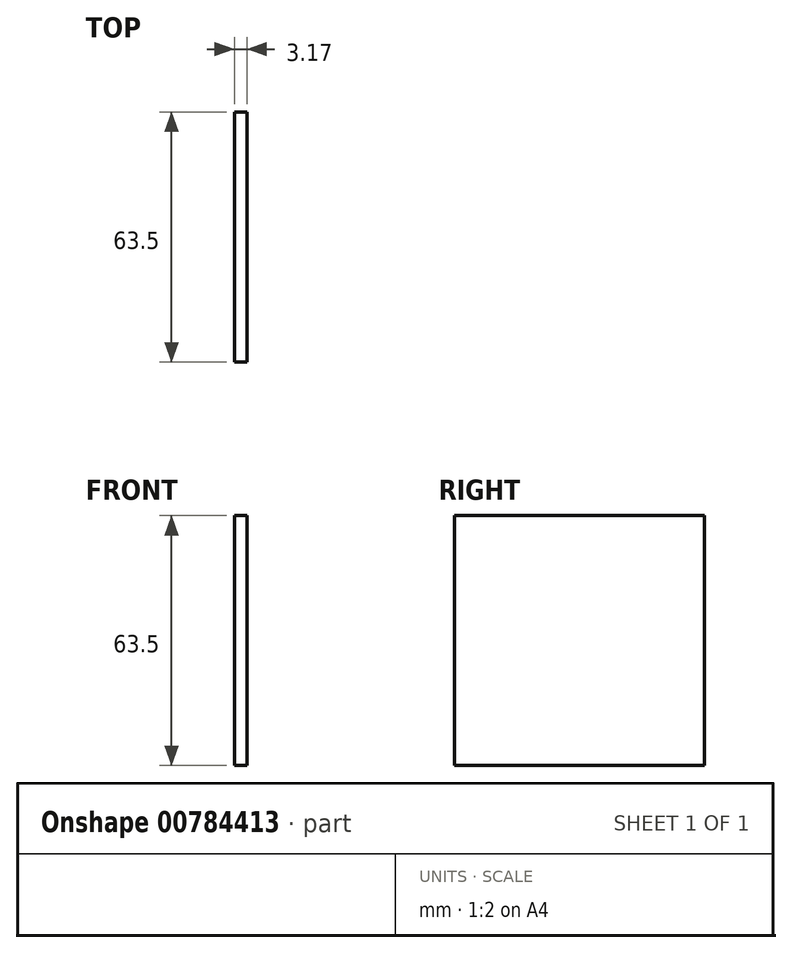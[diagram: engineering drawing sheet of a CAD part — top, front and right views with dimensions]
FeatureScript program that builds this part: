
annotation { "Feature Type Name" : "Feature", "Feature Type Description" : "" }
export const myFeature = defineFeature(function(context is Context, id is Id, definition is map)
    precondition{}
    {
        {
            var Q0;
            Q0=qCreatedBy(makeId("Right.planeOp"),FACE);
            var sketch = newSketch(context, id + "F0", { "sketchPlane" : qUnion([Q0])});
            skLineSegment(sketch, "E0.bottom", {"start": v(-29.8, 31) * mm, "end": v(33.7, 31) * mm});
            skLineSegment(sketch, "E0.top", {"start": v(-29.8, -32.5) * mm, "end": v(33.7, -32.5) * mm});
            skLineSegment(sketch, "E0.left", {"start": v(-29.8, 31) * mm, "end": v(-29.8, -32.5) * mm});
            skLineSegment(sketch, "E0.right", {"start": v(33.7, 31) * mm, "end": v(33.7, -32.5) * mm});
            skSolve(sketch);
        }
        {
            var Q0;
            Q0=makeQuery(id+"F0.imprint","IMPRINT",FACE,{"disambiguationData":[TD([[makeQuery(id+"F0.imprint","IMPRINT",EDGE,{"derivedFrom":sQuery(id+"F0.wireOp",EDGE,"E0.bottom")}),-1.0]])]});
            extrude(context, id + "F1", {"entities" : qUnion([Q0]), "depth" : 3.17 * mm, "offsetDistance" : 25.4 * mm});
        }
    });
